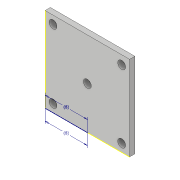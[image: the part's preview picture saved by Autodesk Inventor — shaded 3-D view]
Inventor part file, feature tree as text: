
AUTODESK INVENTOR PART (.ipt)
format: ipt  version: 2019 (Build 230136000, 136)  size: 114,176 bytes
history: native  units: in
note: dims shown in document units (in); Inventor stores cm internally (conversion verified against a paired STEP export)
features: sketch x4, extrude x3
ambient origin geometry x8: Origin, YZ Plane, XZ Plane, XY Plane, X Axis, Y Axis, Z Axis, Center Point
bodies: Solid1 (feature_tree)
feature tree (7):
  extrude  "Extrusion1"  Depth=6.2992in
  extrude  "Extrusion2"  Depth=0.3937in
  sketch  "Sketch3"  dims[d5=0.5906in d6=0.5906in]
  extrude  "Extrusion3"  Depth=0.5906in
  sketch  "Sketch1"  dims[d0=6.2992in d1=6.2992in]
  sketch  "Sketch2"  dims[d2=0.3937in d3=0.0in d4=0.5906in]
  sketch  "Sketch4"  dims[d7=0.5906in d8=0.5906in d9=0.6496in d10=0.5906in d11=0.5906in d12=0.5906in d13=0.5906in d14=0.5906in d15=0.5906in d16=0.3937in d17=0.0in d18=3.1496in d19=3.1496in d20=3.1496in d21=3.1496in d22=3.1496in d23=0.5906in d24=0.3937in d25=0.0in]
